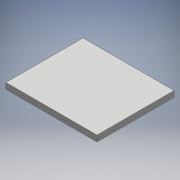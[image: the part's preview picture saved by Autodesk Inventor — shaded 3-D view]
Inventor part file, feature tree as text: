
AUTODESK INVENTOR PART (.ipt)
format: ipt  version: 2018 (Build 220112000, 112)  size: 115,712 bytes
history: native  units: mm
features: extrude x1, pattern_linear x1, sketch x1
ambient origin geometry x8: Origin, YZ Plane, XZ Plane, XY Plane, X Axis, Y Axis, Z Axis, Center Point
bodies: Solid1 (feature_tree)
feature tree (3):
  extrude  "Extrusion1"  Depth=220.0mm
  pattern_linear  "Rectangular Pattern1"  Spacing1=2.0mm  [1 undecoded]
  sketch  "Sketch1"  dims[d0=260.0mm d1=220.0mm d2=2.0mm d3=0.0mm d4=80.0mm d6=15.6mm]
note: 1 required parameter value undecoded (feature->parameter linkage not recoverable at this tier; creation-order binding heuristic only, values carry confidence <= 0.55)
